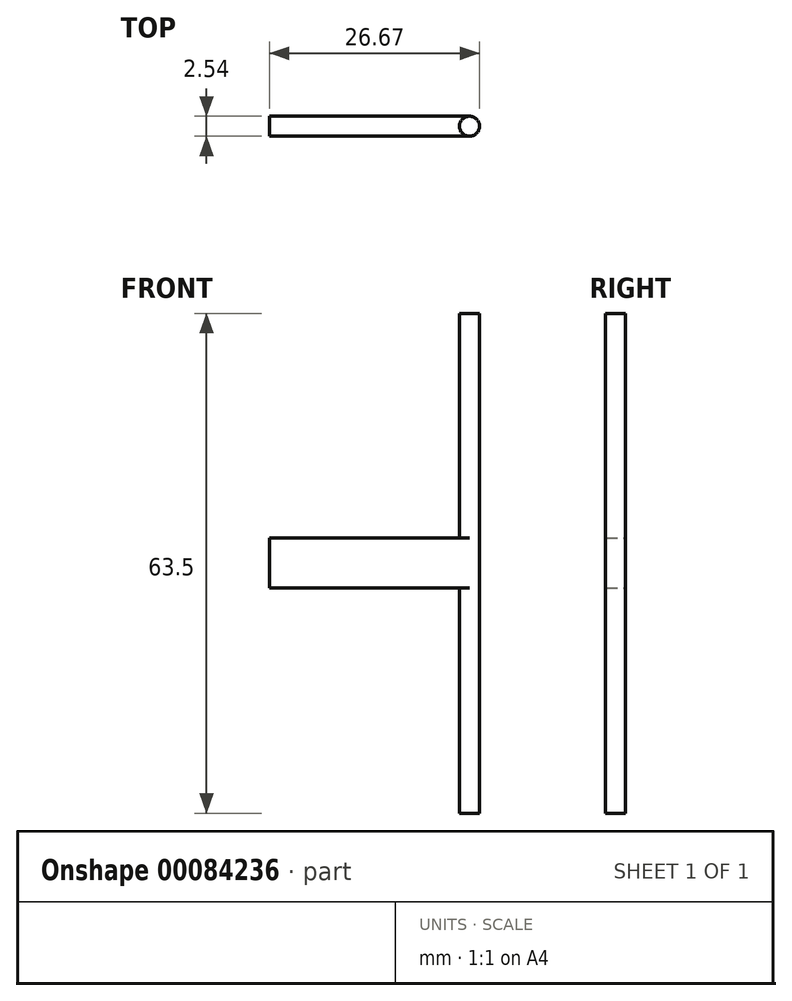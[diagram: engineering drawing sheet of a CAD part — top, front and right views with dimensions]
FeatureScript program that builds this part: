
annotation { "Feature Type Name" : "Feature", "Feature Type Description" : "" }
export const myFeature = defineFeature(function(context is Context, id is Id, definition is map)
    precondition{}
    {
        {
            var Q0;
            Q0=qCreatedBy(makeId("Front.planeOp"),FACE);
            var sketch = newSketch(context, id + "F0", { "sketchPlane" : qUnion([Q0])});
            skLineSegment(sketch, "E0", {"start": v(0, 34.86) * mm, "end": v(0, -28.64) * mm});
            skSolve(sketch);
        }
        {
            var Q0;
            Q0=qCreatedBy(makeId("Top.planeOp"),FACE);
            var sketch = newSketch(context, id + "F1", { "sketchPlane" : qUnion([Q0])});
            skCircle(sketch, "E1", {"center": v(0, 0) * mm, "radius": 1.27 * mm});
            skSolve(sketch);
        }
        {
            var Q0;
            Q0=makeQuery(id+"F1.imprint","IMPRINT",FACE,{"disambiguationData":[TD([[makeQuery(id+"F1.imprint","IMPRINT",EDGE,{"derivedFrom":sQuery(id+"F1.wireOp",EDGE,"E1")}),1.0]])]});
            var Q1;
            Q1=sQuery(id+"F0.wireOp",EDGE,"E0");
            sweep(context, id + "F2", {"profiles" : qUnion([Q0]), "path" : qUnion([Q1])});
        }
        {
            var Q0;
            Q0=qCreatedBy(makeId("Front.planeOp"),FACE);
            var sketch = newSketch(context, id + "F3", { "sketchPlane" : qUnion([Q0])});
            skLineSegment(sketch, "E2.bottom", {"start": v(0, 0) * mm, "end": v(-25.4, 0) * mm});
            skLineSegment(sketch, "E2.top", {"start": v(0, 6.35) * mm, "end": v(-25.4, 6.35) * mm});
            skLineSegment(sketch, "E2.left", {"start": v(0, 0) * mm, "end": v(0, 6.35) * mm});
            skLineSegment(sketch, "E2.right", {"start": v(-25.4, 0) * mm, "end": v(-25.4, 6.35) * mm});
            skSolve(sketch);
        }
        {
            var Q0;
            Q0 = qSketchRegion(id + "F3", true);
            extrude(context, id + "F4", {"entities" : qUnion([Q0]), "operationType" : NewBodyOperationType.ADD, "endBound" : BoundingType.SYMMETRIC, "depth" : 2.54 * mm});
        }
    });
